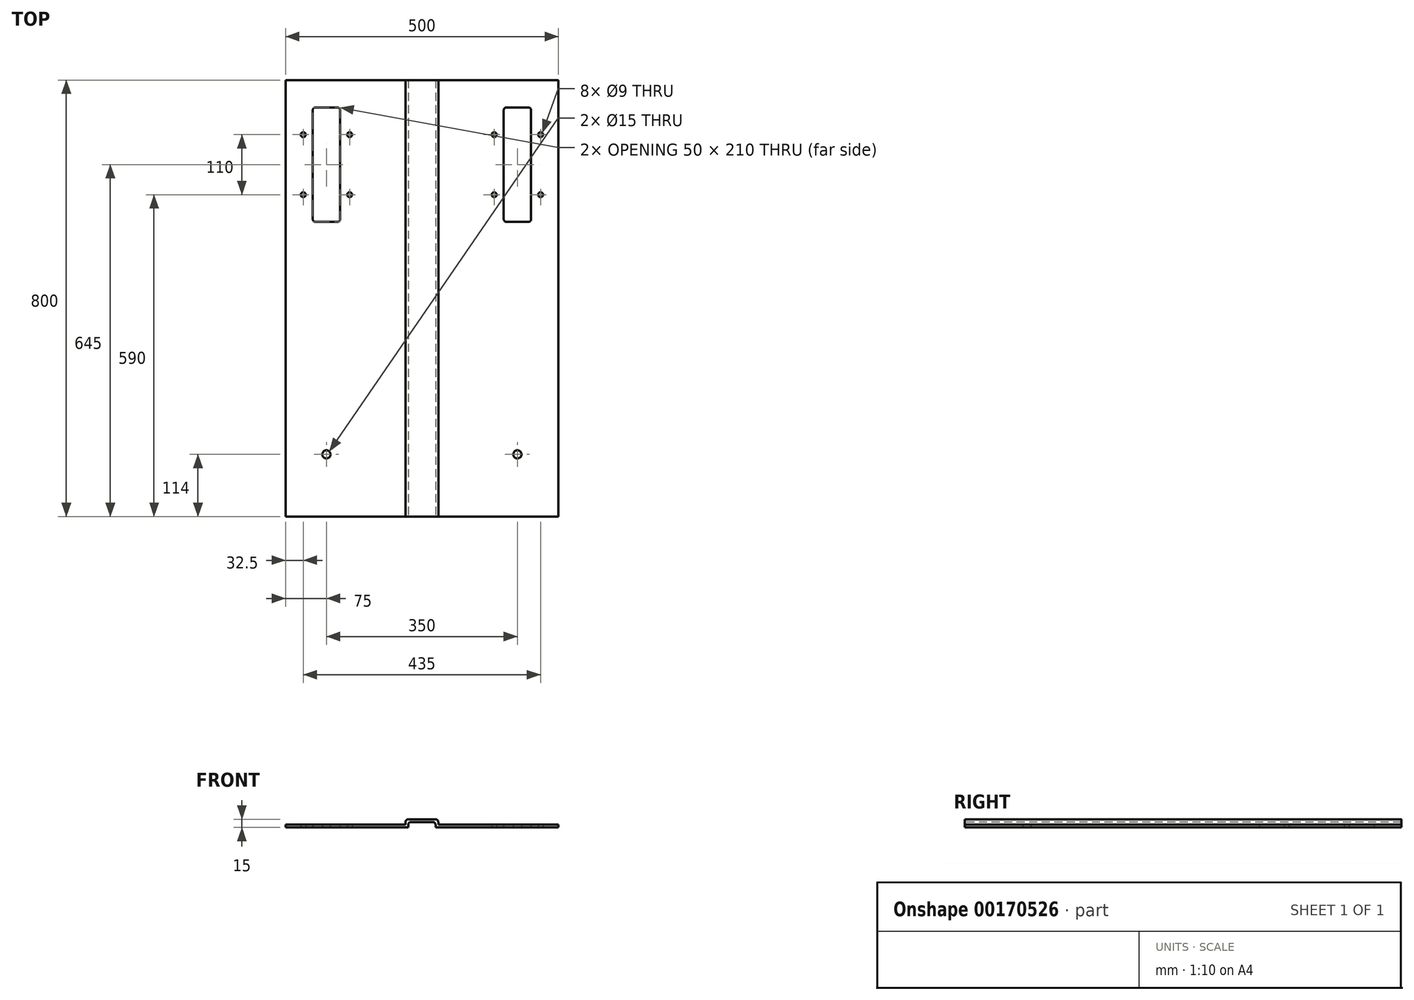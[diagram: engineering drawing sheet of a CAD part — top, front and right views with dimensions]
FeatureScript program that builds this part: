
annotation { "Feature Type Name" : "Feature", "Feature Type Description" : "" }
export const myFeature = defineFeature(function(context is Context, id is Id, definition is map)
    precondition{}
    {
        {
            var Q0;
            Q0=qCreatedBy(makeId("Top.planeOp"),FACE);
            var sketch = newSketch(context, id + "F0", { "sketchPlane" : qUnion([Q0])});
            skLineSegment(sketch, "E0.bottom", {"start": v(-250, 225) * mm, "end": v(250, 225) * mm});
            skLineSegment(sketch, "E0.top", {"start": v(-250, -575) * mm, "end": v(250, -575) * mm});
            skLineSegment(sketch, "E0.left", {"start": v(-250, 225) * mm, "end": v(-250, -575) * mm});
            skLineSegment(sketch, "E0.right", {"start": v(250, 225) * mm, "end": v(250, -575) * mm});
            skLineSegment(sketch, "E1", {"start": v(0, 225) * mm, "end": v(0, -281.03) * mm, "construction": true});
            skLineSegment(sketch, "E2", {"start": v(250, 0) * mm, "end": v(-550, 0) * mm, "construction": true});
            skLineSegment(sketch, "E3.bottom", {"start": v(-195, 175) * mm, "end": v(-155, 175) * mm});
            skLineSegment(sketch, "E3.top", {"start": v(-195, -35) * mm, "end": v(-155, -35) * mm});
            skLineSegment(sketch, "E3.left", {"start": v(-200, 170) * mm, "end": v(-200, -30) * mm});
            skLineSegment(sketch, "E3.right", {"start": v(-150, 170) * mm, "end": v(-150, -30) * mm});
            skCircle(sketch, "E4", {"center": v(-217.5, 125) * mm, "radius": 4.5 * mm});
            skLineSegment(sketch, "E5", {"start": v(-200, 70) * mm, "end": v(-239.44, 70) * mm, "construction": true});
            skLineSegment(sketch, "E6", {"start": v(-175, 175) * mm, "end": v(-175, -66.2) * mm, "construction": true});
            skCircle(sketch, "E7.MirrorC", {"center": v(-217.5, 15) * mm, "radius": 4.5 * mm});
            skCircle(sketch, "E8.MirrorC", {"center": v(-132.5, 125) * mm, "radius": 4.5 * mm});
            skCircle(sketch, "E9.MirrorC", {"center": v(-132.5, 15) * mm, "radius": 4.5 * mm});
            skPoint(sketch, "E10.visualSharp", {"position": v(-200, 175) * mm});
            skArc(sketch, "E10.filletArc", {"start": v(-195, 175) * mm, "mid": v(-198.54, 173.54) * mm, "end": v(-200, 170) * mm});
            skPoint(sketch, "E11.visualSharp", {"position": v(-150, 175) * mm});
            skArc(sketch, "E11.filletArc", {"start": v(-150, 170) * mm, "mid": v(-151.46, 173.54) * mm, "end": v(-155, 175) * mm});
            skPoint(sketch, "E12.visualSharp", {"position": v(-200, -35) * mm});
            skArc(sketch, "E12.filletArc", {"start": v(-200, -30) * mm, "mid": v(-198.54, -33.54) * mm, "end": v(-195, -35) * mm});
            skPoint(sketch, "E13.visualSharp", {"position": v(-150, -35) * mm});
            skArc(sketch, "E13.filletArc", {"start": v(-155, -35) * mm, "mid": v(-151.46, -33.54) * mm, "end": v(-150, -30) * mm});
            skArc(sketch, "E14.MirrorCS", {"start": v(155, -35) * mm, "mid": v(151.46, -33.54) * mm, "end": v(150, -30) * mm});
            skArc(sketch, "E15.MirrorCS", {"start": v(150, 170) * mm, "mid": v(151.46, 173.54) * mm, "end": v(155, 175) * mm});
            skArc(sketch, "E16.MirrorCS", {"start": v(200, -30) * mm, "mid": v(198.54, -33.54) * mm, "end": v(195, -35) * mm});
            skArc(sketch, "E17.MirrorCS", {"start": v(195, 175) * mm, "mid": v(198.54, 173.54) * mm, "end": v(200, 170) * mm});
            skCircle(sketch, "E18.MirrorC", {"center": v(217.5, 15) * mm, "radius": 4.5 * mm});
            skCircle(sketch, "E19.MirrorC", {"center": v(132.5, 125) * mm, "radius": 4.5 * mm});
            skCircle(sketch, "E20.MirrorC", {"center": v(132.5, 15) * mm, "radius": 4.5 * mm});
            skCircle(sketch, "E21.MirrorC", {"center": v(217.5, 125) * mm, "radius": 4.5 * mm});
            skPoint(sketch, "E22.MirrorP", {"position": v(200, -35) * mm});
            skLineSegment(sketch, "E23.MirrorCS", {"start": v(195, 175) * mm, "end": v(155, 175) * mm});
            skLineSegment(sketch, "E24.MirrorCS", {"start": v(195, -35) * mm, "end": v(155, -35) * mm});
            skPoint(sketch, "E25.MirrorP", {"position": v(150, -35) * mm});
            skPoint(sketch, "E26.MirrorP", {"position": v(150, 175) * mm});
            skLineSegment(sketch, "E27.MirrorCS", {"start": v(200, 170) * mm, "end": v(200, -30) * mm});
            skLineSegment(sketch, "E28.MirrorCS", {"start": v(150, 170) * mm, "end": v(150, -30) * mm});
            skPoint(sketch, "E29.MirrorP", {"position": v(200, 175) * mm});
            skLineSegment(sketch, "E30", {"start": v(-175, -428.1) * mm, "end": v(-175, -642.63) * mm, "construction": true});
            skCircle(sketch, "E31", {"center": v(-175, -461) * mm, "radius": 7.5 * mm});
            skCircle(sketch, "E32.MirrorC", {"center": v(175, -461) * mm, "radius": 7.5 * mm});
            skSolve(sketch);
        }
        {
            var Q0;
            Q0=makeQuery(id+"F0.imprint","IMPRINT",FACE,{"disambiguationData":[TD([[makeQuery(id+"F0.imprint","IMPRINT",EDGE,{"derivedFrom":sQuery(id+"F0.wireOp",EDGE,"E0.bottom")}),-1.0]])]});
            extrude(context, id + "F1", {"entities" : qUnion([Q0]), "depth" : 5 * mm});
        }
        {
            var Q0;
            Q0=makeQuery(id+"F1.opExtrude","SWEPT_FACE",FACE,{"disambiguationData":[OSD([sQuery(id+"F0.wireOp",EDGE,"E0.top")])]});
            var sketch = newSketch(context, id + "F2", { "sketchPlane" : qUnion([Q0])});
            skLineSegment(sketch, "E33.top", {"start": v(0, 15) * mm, "end": v(-25, 15) * mm});
            skLineSegment(sketch, "E33.right", {"start": v(-30, 0) * mm, "end": v(-30, 10) * mm});
            skArc(sketch, "E34.filletArc", {"start": v(-25, 15) * mm, "mid": v(-28.54, 13.54) * mm, "end": v(-30, 10) * mm});
            skArc(sketch, "E35.MirrorCS", {"start": v(25, 15) * mm, "mid": v(28.54, 13.54) * mm, "end": v(30, 10) * mm});
            skLineSegment(sketch, "E36.MirrorCS", {"start": v(0, 15) * mm, "end": v(25, 15) * mm});
            skLineSegment(sketch, "E37.MirrorCS", {"start": v(30, 0) * mm, "end": v(30, 10) * mm});
            skLineSegment(sketch, "E38", {"start": v(-30, 0) * mm, "end": v(30, 0) * mm});
            skSolve(sketch);
        }
        {
            var Q0;
            Q0=makeQuery(id+"F2.imprint","IMPRINT",FACE,{"disambiguationData":[TD([[makeQuery(id+"F2.imprint","IMPRINT",EDGE,{"derivedFrom":sQuery(id+"F2.wireOp",EDGE,"E33.top")}),1.0]])]});
            var Q1;
            Q1=makeQuery(id+"F1.opExtrude","SWEPT_FACE",FACE,{"disambiguationData":[OSD([sQuery(id+"F0.wireOp",EDGE,"E0.bottom")])]});
            extrude(context, id + "F3", {"entities" : qUnion([Q0]), "operationType" : NewBodyOperationType.ADD, "endBound" : BoundingType.UP_TO_SURFACE, "oppositeDirection" : true, "endBoundEntityFace" : qUnion([Q1]), "depth" : 25 * mm});
        }
        {
            var Q0;
            {var subQ0=sQuery(id+"F0.wireOp",EDGE,"E0.top");Q0=makeQuery(id+"F3.boolean.opBoolean","MERGE",FACE,{"derivedFrom":[makeQuery(id+"F1.opExtrude","SWEPT_FACE",FACE,{"disambiguationData":[OSD([subQ0])]}),makeQuery(id+"F3.opExtrude","CAP_FACE",FACE,{"disambiguationData":[OSD([subQ0,sQuery(id+"F2.wireOp",EDGE,"E33.top"),sQuery(id+"F2.wireOp",EDGE,"E33.right"),sQuery(id+"F2.wireOp",EDGE,"E34.filletArc"),sQuery(id+"F2.wireOp",EDGE,"E35.MirrorCS"),sQuery(id+"F2.wireOp",EDGE,"E36.MirrorCS"),sQuery(id+"F2.wireOp",EDGE,"E37.MirrorCS")])],"isStart":true})]});}
            var sketch = newSketch(context, id + "F4", { "sketchPlane" : qUnion([Q0])});
            skLineSegment(sketch, "E39", {"start": v(-25, 0) * mm, "end": v(-25, 5) * mm});
            skLineSegment(sketch, "E40", {"start": v(25, 0) * mm, "end": v(25, 5) * mm});
            skLineSegment(sketch, "E41.0", {"start": v(-20, 10) * mm, "end": v(20, 10) * mm});
            skArc(sketch, "E42.filletArc", {"start": v(-20, 10) * mm, "mid": v(-23.54, 8.54) * mm, "end": v(-25, 5) * mm});
            skArc(sketch, "E43.filletArc", {"start": v(25, 5) * mm, "mid": v(23.54, 8.54) * mm, "end": v(20, 10) * mm});
            skLineSegment(sketch, "E44", {"start": v(-25, 0) * mm, "end": v(25, 0) * mm});
            skSolve(sketch);
        }
        {
            var Q0;
            Q0=makeQuery(id+"F4.imprint","IMPRINT",FACE,{"disambiguationData":[TD([[makeQuery(id+"F4.imprint","IMPRINT",EDGE,{"derivedFrom":sQuery(id+"F4.wireOp",EDGE,"E39")}),-1.0]])]});
            extrude(context, id + "F5", {"entities" : qUnion([Q0]), "operationType" : NewBodyOperationType.REMOVE, "endBound" : BoundingType.THROUGH_ALL, "oppositeDirection" : true, "depth" : 25 * mm});
        }
    });
